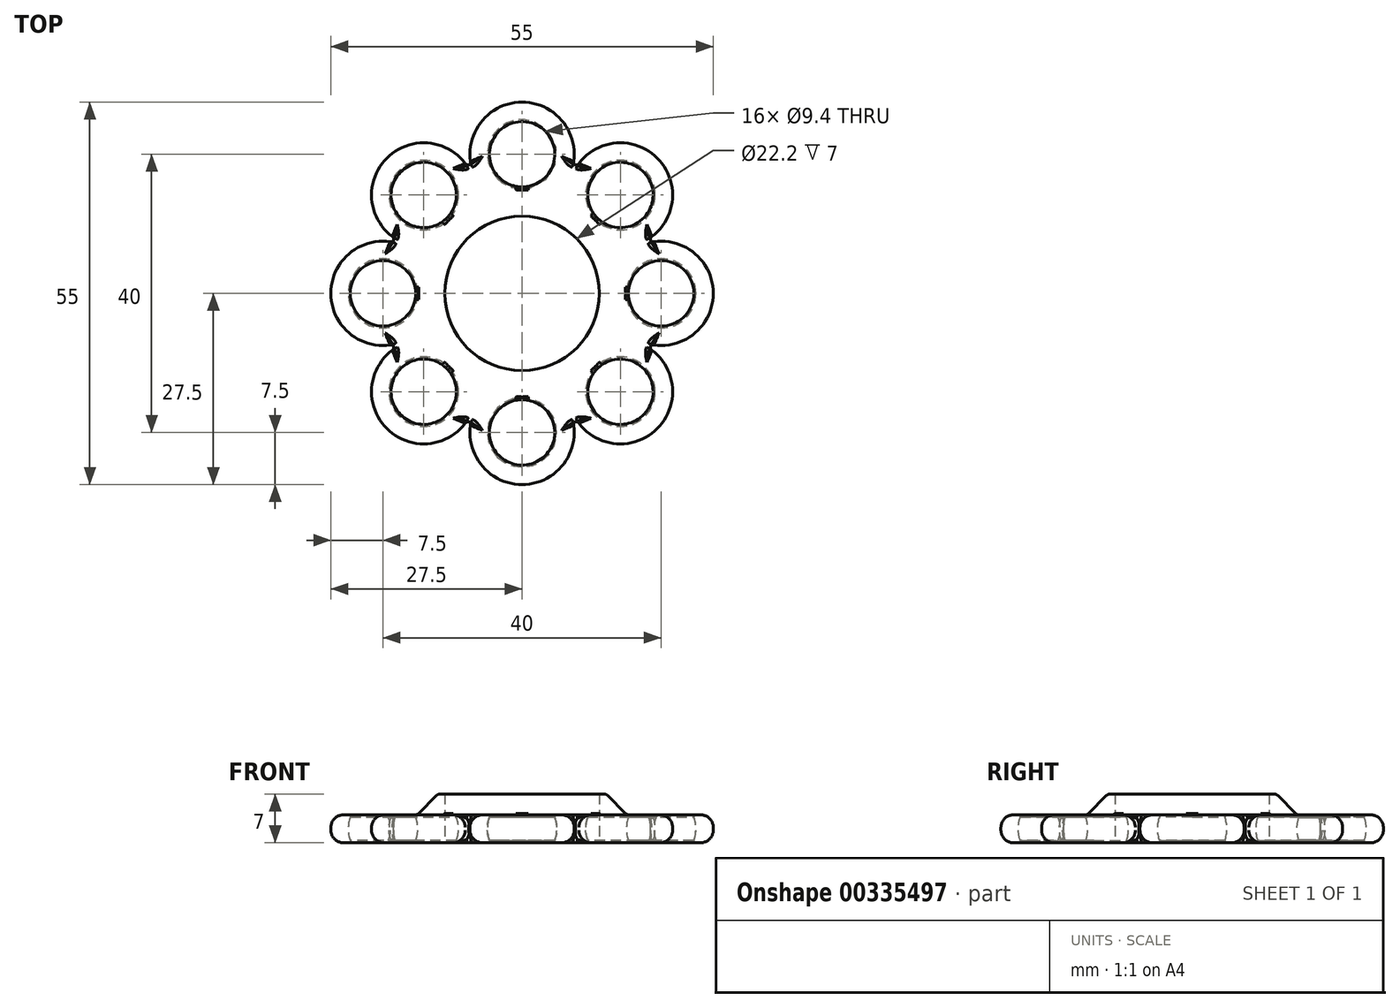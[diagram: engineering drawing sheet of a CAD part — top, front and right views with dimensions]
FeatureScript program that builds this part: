
annotation { "Feature Type Name" : "Feature", "Feature Type Description" : "" }
export const myFeature = defineFeature(function(context is Context, id is Id, definition is map)
    precondition{}
    {
        {
            var Q0;
            Q0=qCreatedBy(makeId("Top.planeOp"),FACE);
            var sketch = newSketch(context, id + "F0", { "sketchPlane" : qUnion([Q0])});
            skCircle(sketch, "E0", {"center": v(0, 0) * mm, "radius": 11.1 * mm});
            skCircle(sketch, "E1", {"center": v(0, 20) * mm, "radius": 4.7 * mm});
            skCircle(sketch, "E2.1.0", {"center": v(-14.14, 14.14) * mm, "radius": 4.7 * mm});
            skCircle(sketch, "E2.2.0", {"center": v(-20, 0) * mm, "radius": 4.7 * mm});
            skCircle(sketch, "E2.3.0", {"center": v(-14.14, -14.14) * mm, "radius": 4.7 * mm});
            skCircle(sketch, "E2.4.0", {"center": v(0, -20) * mm, "radius": 4.7 * mm});
            skCircle(sketch, "E2.5.0", {"center": v(14.14, -14.14) * mm, "radius": 4.7 * mm});
            skCircle(sketch, "E2.6.0", {"center": v(20, 0) * mm, "radius": 4.7 * mm});
            skCircle(sketch, "E2.7.0", {"center": v(14.14, 14.14) * mm, "radius": 4.7 * mm});
            skCircle(sketch, "E3", {"center": v(0, 20) * mm, "radius": 7.5 * mm});
            skCircle(sketch, "E4.1.0", {"center": v(-14.14, 14.14) * mm, "radius": 7.5 * mm});
            skCircle(sketch, "E4.2.0", {"center": v(-20, 0) * mm, "radius": 7.5 * mm});
            skCircle(sketch, "E4.3.0", {"center": v(-14.14, -14.14) * mm, "radius": 7.5 * mm});
            skCircle(sketch, "E4.4.0", {"center": v(0, -20) * mm, "radius": 7.5 * mm});
            skCircle(sketch, "E4.5.0", {"center": v(14.14, -14.14) * mm, "radius": 7.5 * mm});
            skCircle(sketch, "E4.6.0", {"center": v(20, 0) * mm, "radius": 7.5 * mm});
            skCircle(sketch, "E4.7.0", {"center": v(14.14, 14.14) * mm, "radius": 7.5 * mm});
            skCircle(sketch, "E5", {"center": v(0, 0) * mm, "radius": 20 * mm});
            skSolve(sketch);
        }
        {
            var Q0;
            Q0=makeQuery(id+"F0.imprint","IMPRINT",FACE,{"disambiguationData":[TD([[makeQuery(id+"F0.imprint","IMPRINT",EDGE,{"derivedFrom":sQuery(id+"F0.wireOp",EDGE,"E0")}),-1.0]])]});
            var Q1;
            {var subQ0=sQuery(id+"F0.wireOp",EDGE,"E5");var subQ1=sQuery(id+"F0.wireOp",EDGE,"E2.3.0");var subQ2=makeQuery(id+"F0.imprint","INTERSECT",VERTEX,{"disambiguationData":[OD(0.0)],"derivedFrom":[subQ1,subQ0]});Q1=makeQuery(id+"F0.imprint","IMPRINT",FACE,{"disambiguationData":[TD([[makeQuery(id+"F0.imprint","IMPRINT",EDGE,{"disambiguationData":[TD([[subQ2,-1.0]])],"derivedFrom":subQ1}),-1.0]])]});}
            var Q2;
            {var subQ0=sQuery(id+"F0.wireOp",EDGE,"E5");var subQ1=sQuery(id+"F0.wireOp",EDGE,"E2.3.0");var subQ2=makeQuery(id+"F0.imprint","INTERSECT",VERTEX,{"disambiguationData":[OD(0.0)],"derivedFrom":[subQ1,subQ0]});Q2=makeQuery(id+"F0.imprint","IMPRINT",FACE,{"disambiguationData":[TD([[makeQuery(id+"F0.imprint","IMPRINT",EDGE,{"disambiguationData":[TD([[subQ2,1.0]])],"derivedFrom":subQ1}),-1.0]])]});}
            var Q3;
            {var subQ0=sQuery(id+"F0.wireOp",EDGE,"E5");var subQ1=sQuery(id+"F0.wireOp",EDGE,"E2.2.0");var subQ2=makeQuery(id+"F0.imprint","INTERSECT",VERTEX,{"disambiguationData":[OD(0.0)],"derivedFrom":[subQ1,subQ0]});Q3=makeQuery(id+"F0.imprint","IMPRINT",FACE,{"disambiguationData":[TD([[makeQuery(id+"F0.imprint","IMPRINT",EDGE,{"disambiguationData":[TD([[subQ2,1.0]])],"derivedFrom":subQ1}),-1.0]])]});}
            var Q4;
            {var subQ0=sQuery(id+"F0.wireOp",EDGE,"E5");var subQ1=sQuery(id+"F0.wireOp",EDGE,"E2.2.0");var subQ2=makeQuery(id+"F0.imprint","INTERSECT",VERTEX,{"disambiguationData":[OD(0.0)],"derivedFrom":[subQ1,subQ0]});Q4=makeQuery(id+"F0.imprint","IMPRINT",FACE,{"disambiguationData":[TD([[makeQuery(id+"F0.imprint","IMPRINT",EDGE,{"disambiguationData":[TD([[subQ2,-1.0]])],"derivedFrom":subQ1}),-1.0]])]});}
            var Q5;
            {var subQ0=sQuery(id+"F0.wireOp",EDGE,"E5");var subQ1=sQuery(id+"F0.wireOp",EDGE,"E2.1.0");var subQ2=makeQuery(id+"F0.imprint","INTERSECT",VERTEX,{"disambiguationData":[OD(0.0)],"derivedFrom":[subQ1,subQ0]});Q5=makeQuery(id+"F0.imprint","IMPRINT",FACE,{"disambiguationData":[TD([[makeQuery(id+"F0.imprint","IMPRINT",EDGE,{"disambiguationData":[TD([[subQ2,-1.0]])],"derivedFrom":subQ1}),-1.0]])]});}
            var Q6;
            {var subQ0=sQuery(id+"F0.wireOp",EDGE,"E5");var subQ1=sQuery(id+"F0.wireOp",EDGE,"E2.1.0");var subQ2=makeQuery(id+"F0.imprint","INTERSECT",VERTEX,{"disambiguationData":[OD(0.0)],"derivedFrom":[subQ1,subQ0]});Q6=makeQuery(id+"F0.imprint","IMPRINT",FACE,{"disambiguationData":[TD([[makeQuery(id+"F0.imprint","IMPRINT",EDGE,{"disambiguationData":[TD([[subQ2,1.0]])],"derivedFrom":subQ1}),-1.0]])]});}
            var Q7;
            {var subQ0=sQuery(id+"F0.wireOp",EDGE,"E5");var subQ1=sQuery(id+"F0.wireOp",EDGE,"E1");var subQ2=makeQuery(id+"F0.imprint","INTERSECT",VERTEX,{"disambiguationData":[OD(0.0)],"derivedFrom":[subQ1,subQ0]});Q7=makeQuery(id+"F0.imprint","IMPRINT",FACE,{"disambiguationData":[TD([[makeQuery(id+"F0.imprint","IMPRINT",EDGE,{"disambiguationData":[TD([[subQ2,1.0]])],"derivedFrom":subQ1}),-1.0]])]});}
            var Q8;
            {var subQ0=sQuery(id+"F0.wireOp",EDGE,"E5");var subQ1=sQuery(id+"F0.wireOp",EDGE,"E1");var subQ2=makeQuery(id+"F0.imprint","INTERSECT",VERTEX,{"disambiguationData":[OD(0.0)],"derivedFrom":[subQ1,subQ0]});Q8=makeQuery(id+"F0.imprint","IMPRINT",FACE,{"disambiguationData":[TD([[makeQuery(id+"F0.imprint","IMPRINT",EDGE,{"disambiguationData":[TD([[subQ2,-1.0]])],"derivedFrom":subQ1}),-1.0]])]});}
            var Q9;
            {var subQ0=sQuery(id+"F0.wireOp",EDGE,"E5");var subQ1=sQuery(id+"F0.wireOp",EDGE,"E2.7.0");var subQ2=makeQuery(id+"F0.imprint","INTERSECT",VERTEX,{"disambiguationData":[OD(0.0)],"derivedFrom":[subQ1,subQ0]});Q9=makeQuery(id+"F0.imprint","IMPRINT",FACE,{"disambiguationData":[TD([[makeQuery(id+"F0.imprint","IMPRINT",EDGE,{"disambiguationData":[TD([[subQ2,1.0]])],"derivedFrom":subQ1}),-1.0]])]});}
            var Q10;
            {var subQ0=sQuery(id+"F0.wireOp",EDGE,"E5");var subQ1=sQuery(id+"F0.wireOp",EDGE,"E2.7.0");var subQ2=makeQuery(id+"F0.imprint","INTERSECT",VERTEX,{"disambiguationData":[OD(0.0)],"derivedFrom":[subQ1,subQ0]});Q10=makeQuery(id+"F0.imprint","IMPRINT",FACE,{"disambiguationData":[TD([[makeQuery(id+"F0.imprint","IMPRINT",EDGE,{"disambiguationData":[TD([[subQ2,-1.0]])],"derivedFrom":subQ1}),-1.0]])]});}
            var Q11;
            {var subQ0=sQuery(id+"F0.wireOp",EDGE,"E5");var subQ1=sQuery(id+"F0.wireOp",EDGE,"E2.6.0");var subQ2=makeQuery(id+"F0.imprint","INTERSECT",VERTEX,{"disambiguationData":[OD(0.0)],"derivedFrom":[subQ1,subQ0]});Q11=makeQuery(id+"F0.imprint","IMPRINT",FACE,{"disambiguationData":[TD([[makeQuery(id+"F0.imprint","IMPRINT",EDGE,{"disambiguationData":[TD([[subQ2,-1.0]])],"derivedFrom":subQ1}),-1.0]])]});}
            var Q12;
            {var subQ0=sQuery(id+"F0.wireOp",EDGE,"E5");var subQ1=sQuery(id+"F0.wireOp",EDGE,"E2.6.0");var subQ2=makeQuery(id+"F0.imprint","INTERSECT",VERTEX,{"disambiguationData":[OD(0.0)],"derivedFrom":[subQ1,subQ0]});Q12=makeQuery(id+"F0.imprint","IMPRINT",FACE,{"disambiguationData":[TD([[makeQuery(id+"F0.imprint","IMPRINT",EDGE,{"disambiguationData":[TD([[subQ2,1.0]])],"derivedFrom":subQ1}),-1.0]])]});}
            var Q13;
            {var subQ0=sQuery(id+"F0.wireOp",EDGE,"E5");var subQ1=sQuery(id+"F0.wireOp",EDGE,"E2.5.0");var subQ2=makeQuery(id+"F0.imprint","INTERSECT",VERTEX,{"disambiguationData":[OD(0.0)],"derivedFrom":[subQ1,subQ0]});Q13=makeQuery(id+"F0.imprint","IMPRINT",FACE,{"disambiguationData":[TD([[makeQuery(id+"F0.imprint","IMPRINT",EDGE,{"disambiguationData":[TD([[subQ2,1.0]])],"derivedFrom":subQ1}),-1.0]])]});}
            var Q14;
            {var subQ0=sQuery(id+"F0.wireOp",EDGE,"E5");var subQ1=sQuery(id+"F0.wireOp",EDGE,"E2.5.0");var subQ2=makeQuery(id+"F0.imprint","INTERSECT",VERTEX,{"disambiguationData":[OD(0.0)],"derivedFrom":[subQ1,subQ0]});Q14=makeQuery(id+"F0.imprint","IMPRINT",FACE,{"disambiguationData":[TD([[makeQuery(id+"F0.imprint","IMPRINT",EDGE,{"disambiguationData":[TD([[subQ2,-1.0]])],"derivedFrom":subQ1}),-1.0]])]});}
            var Q15;
            {var subQ0=sQuery(id+"F0.wireOp",EDGE,"E5");var subQ1=sQuery(id+"F0.wireOp",EDGE,"E2.4.0");var subQ2=makeQuery(id+"F0.imprint","INTERSECT",VERTEX,{"disambiguationData":[OD(0.0)],"derivedFrom":[subQ1,subQ0]});Q15=makeQuery(id+"F0.imprint","IMPRINT",FACE,{"disambiguationData":[TD([[makeQuery(id+"F0.imprint","IMPRINT",EDGE,{"disambiguationData":[TD([[subQ2,1.0]])],"derivedFrom":subQ1}),-1.0]])]});}
            var Q16;
            {var subQ0=sQuery(id+"F0.wireOp",EDGE,"E5");var subQ1=sQuery(id+"F0.wireOp",EDGE,"E2.4.0");var subQ2=makeQuery(id+"F0.imprint","INTERSECT",VERTEX,{"disambiguationData":[OD(0.0)],"derivedFrom":[subQ1,subQ0]});Q16=makeQuery(id+"F0.imprint","IMPRINT",FACE,{"disambiguationData":[TD([[makeQuery(id+"F0.imprint","IMPRINT",EDGE,{"disambiguationData":[TD([[subQ2,-1.0]])],"derivedFrom":subQ1}),-1.0]])]});}
            extrude(context, id + "F1", {"entities" : qUnion([Q0, Q1, Q2, Q3, Q4, Q5, Q6, Q7, Q8, Q9, Q10, Q11, Q12, Q13, Q14, Q15, Q16]), "depth" : 2 * mm, "hasSecondDirection" : true, "secondDirectionOppositeDirection" : true, "secondDirectionDepth" : 2 * mm});
        }
        {
            var Q0;
            Q0=makeQuery(id+"F1.opExtrude","CAP_EDGE",EDGE,{"disambiguationData":[OSD([sQuery(id+"F0.wireOp",EDGE,"E4.7.0")])],"isStart":false});
            var Q1;
            Q1=makeQuery(id+"F1.opExtrude","CAP_EDGE",EDGE,{"disambiguationData":[OSD([sQuery(id+"F0.wireOp",EDGE,"E4.7.0")])],"isStart":true});
            var Q2;
            Q2=makeQuery(id+"F1.opExtrude","CAP_EDGE",EDGE,{"disambiguationData":[OSD([sQuery(id+"F0.wireOp",EDGE,"E4.3.0")])],"isStart":true});
            var Q3;
            Q3=makeQuery(id+"F1.opExtrude","CAP_EDGE",EDGE,{"disambiguationData":[OSD([sQuery(id+"F0.wireOp",EDGE,"E4.3.0")])],"isStart":false});
            var Q4;
            Q4=makeQuery(id+"F1.opExtrude","CAP_EDGE",EDGE,{"disambiguationData":[OSD([sQuery(id+"F0.wireOp",EDGE,"E4.2.0")])],"isStart":false});
            var Q5;
            Q5=makeQuery(id+"F1.opExtrude","CAP_EDGE",EDGE,{"disambiguationData":[OSD([sQuery(id+"F0.wireOp",EDGE,"E4.2.0")])],"isStart":true});
            var Q6;
            Q6=makeQuery(id+"F1.opExtrude","CAP_EDGE",EDGE,{"disambiguationData":[OSD([sQuery(id+"F0.wireOp",EDGE,"E4.4.0")])],"isStart":false});
            var Q7;
            Q7=makeQuery(id+"F1.opExtrude","CAP_EDGE",EDGE,{"disambiguationData":[OSD([sQuery(id+"F0.wireOp",EDGE,"E4.4.0")])],"isStart":true});
            var Q8;
            Q8=makeQuery(id+"F1.opExtrude","CAP_EDGE",EDGE,{"disambiguationData":[OSD([sQuery(id+"F0.wireOp",EDGE,"E4.5.0")])],"isStart":false});
            var Q9;
            Q9=makeQuery(id+"F1.opExtrude","CAP_EDGE",EDGE,{"disambiguationData":[OSD([sQuery(id+"F0.wireOp",EDGE,"E4.5.0")])],"isStart":true});
            var Q10;
            Q10=makeQuery(id+"F1.opExtrude","CAP_EDGE",EDGE,{"disambiguationData":[OSD([sQuery(id+"F0.wireOp",EDGE,"E4.6.0")])],"isStart":false});
            var Q11;
            Q11=makeQuery(id+"F1.opExtrude","CAP_EDGE",EDGE,{"disambiguationData":[OSD([sQuery(id+"F0.wireOp",EDGE,"E4.6.0")])],"isStart":true});
            var Q12;
            Q12=makeQuery(id+"F1.opExtrude","CAP_EDGE",EDGE,{"disambiguationData":[OSD([sQuery(id+"F0.wireOp",EDGE,"E3")])],"isStart":true});
            var Q13;
            Q13=makeQuery(id+"F1.opExtrude","CAP_EDGE",EDGE,{"disambiguationData":[OSD([sQuery(id+"F0.wireOp",EDGE,"E3")])],"isStart":false});
            var Q14;
            Q14=makeQuery(id+"F1.opExtrude","CAP_EDGE",EDGE,{"disambiguationData":[OSD([sQuery(id+"F0.wireOp",EDGE,"E4.1.0")])],"isStart":true});
            var Q15;
            Q15=makeQuery(id+"F1.opExtrude","CAP_EDGE",EDGE,{"disambiguationData":[OSD([sQuery(id+"F0.wireOp",EDGE,"E4.1.0")])],"isStart":false});
            fillet(context, id + "F2", {"entities" : qUnion([Q0, Q1, Q2, Q3, Q4, Q5, Q6, Q7, Q8, Q9, Q10, Q11, Q12, Q13, Q14, Q15]), "radius" : 1.8 * mm, "tangentPropagation" : true, "allowEdgeOverflow" : false});
        }
        {
            var Q0;
            {var subQ0=sQuery(id+"F0.wireOp",EDGE,"E5");var subQ1=sQuery(id+"F0.wireOp",EDGE,"E4.4.0");Q0=makeQuery(id+"F1.opExtrude","SWEPT_EDGE",EDGE,{"disambiguationData":[OSD([subQ1,subQ0]),TDD([makeQuery(id+"F0.imprint","INTERSECT",VERTEX,{"disambiguationData":[OD(0.0)],"derivedFrom":[subQ1,subQ0]})])]});}
            var Q1;
            {var subQ0=sQuery(id+"F0.wireOp",EDGE,"E5");var subQ1=sQuery(id+"F0.wireOp",EDGE,"E4.2.0");Q1=makeQuery(id+"F1.opExtrude","SWEPT_EDGE",EDGE,{"disambiguationData":[OSD([subQ1,subQ0]),TDD([makeQuery(id+"F0.imprint","INTERSECT",VERTEX,{"disambiguationData":[OD(1.0)],"derivedFrom":[subQ1,subQ0]})])]});}
            var Q2;
            {var subQ0=sQuery(id+"F0.wireOp",EDGE,"E5");var subQ1=sQuery(id+"F0.wireOp",EDGE,"E4.2.0");Q2=makeQuery(id+"F1.opExtrude","SWEPT_EDGE",EDGE,{"disambiguationData":[OSD([subQ1,subQ0]),TDD([makeQuery(id+"F0.imprint","INTERSECT",VERTEX,{"disambiguationData":[OD(0.0)],"derivedFrom":[subQ1,subQ0]})])]});}
            var Q3;
            {var subQ0=sQuery(id+"F0.wireOp",EDGE,"E5");var subQ1=sQuery(id+"F0.wireOp",EDGE,"E3");Q3=makeQuery(id+"F1.opExtrude","SWEPT_EDGE",EDGE,{"disambiguationData":[OSD([subQ1,subQ0]),TDD([makeQuery(id+"F0.imprint","INTERSECT",VERTEX,{"disambiguationData":[OD(1.0)],"derivedFrom":[subQ1,subQ0]})])]});}
            var Q4;
            {var subQ0=sQuery(id+"F0.wireOp",EDGE,"E5");var subQ1=sQuery(id+"F0.wireOp",EDGE,"E4.7.0");Q4=makeQuery(id+"F1.opExtrude","SWEPT_EDGE",EDGE,{"disambiguationData":[OSD([subQ1,subQ0]),TDD([makeQuery(id+"F0.imprint","INTERSECT",VERTEX,{"disambiguationData":[OD(1.0)],"derivedFrom":[subQ1,subQ0]})])]});}
            var Q5;
            {var subQ0=sQuery(id+"F0.wireOp",EDGE,"E5");var subQ1=sQuery(id+"F0.wireOp",EDGE,"E4.1.0");Q5=makeQuery(id+"F1.opExtrude","SWEPT_EDGE",EDGE,{"disambiguationData":[OSD([subQ1,subQ0]),TDD([makeQuery(id+"F0.imprint","INTERSECT",VERTEX,{"disambiguationData":[OD(1.0)],"derivedFrom":[subQ1,subQ0]})])]});}
            var Q6;
            {var subQ0=sQuery(id+"F0.wireOp",EDGE,"E5");var subQ1=sQuery(id+"F0.wireOp",EDGE,"E4.3.0");Q6=makeQuery(id+"F1.opExtrude","SWEPT_EDGE",EDGE,{"disambiguationData":[OSD([subQ1,subQ0]),TDD([makeQuery(id+"F0.imprint","INTERSECT",VERTEX,{"disambiguationData":[OD(0.0)],"derivedFrom":[subQ1,subQ0]})])]});}
            var Q7;
            {var subQ0=sQuery(id+"F0.wireOp",EDGE,"E5");var subQ1=sQuery(id+"F0.wireOp",EDGE,"E4.1.0");Q7=makeQuery(id+"F1.opExtrude","SWEPT_EDGE",EDGE,{"disambiguationData":[OSD([subQ1,subQ0]),TDD([makeQuery(id+"F0.imprint","INTERSECT",VERTEX,{"disambiguationData":[OD(0.0)],"derivedFrom":[subQ1,subQ0]})])]});}
            var Q8;
            {var subQ0=sQuery(id+"F0.wireOp",EDGE,"E5");var subQ1=sQuery(id+"F0.wireOp",EDGE,"E3");Q8=makeQuery(id+"F1.opExtrude","SWEPT_EDGE",EDGE,{"disambiguationData":[OSD([subQ1,subQ0]),TDD([makeQuery(id+"F0.imprint","INTERSECT",VERTEX,{"disambiguationData":[OD(0.0)],"derivedFrom":[subQ1,subQ0]})])]});}
            var Q9;
            {var subQ0=sQuery(id+"F0.wireOp",EDGE,"E5");var subQ1=sQuery(id+"F0.wireOp",EDGE,"E4.6.0");Q9=makeQuery(id+"F1.opExtrude","SWEPT_EDGE",EDGE,{"disambiguationData":[OSD([subQ1,subQ0]),TDD([makeQuery(id+"F0.imprint","INTERSECT",VERTEX,{"disambiguationData":[OD(0.0)],"derivedFrom":[subQ1,subQ0]})])]});}
            var Q10;
            {var subQ0=sQuery(id+"F0.wireOp",EDGE,"E5");var subQ1=sQuery(id+"F0.wireOp",EDGE,"E4.7.0");Q10=makeQuery(id+"F1.opExtrude","SWEPT_EDGE",EDGE,{"disambiguationData":[OSD([subQ1,subQ0]),TDD([makeQuery(id+"F0.imprint","INTERSECT",VERTEX,{"disambiguationData":[OD(0.0)],"derivedFrom":[subQ1,subQ0]})])]});}
            var Q11;
            {var subQ0=sQuery(id+"F0.wireOp",EDGE,"E5");var subQ1=sQuery(id+"F0.wireOp",EDGE,"E4.6.0");Q11=makeQuery(id+"F1.opExtrude","SWEPT_EDGE",EDGE,{"disambiguationData":[OSD([subQ1,subQ0]),TDD([makeQuery(id+"F0.imprint","INTERSECT",VERTEX,{"disambiguationData":[OD(1.0)],"derivedFrom":[subQ1,subQ0]})])]});}
            var Q12;
            {var subQ0=sQuery(id+"F0.wireOp",EDGE,"E5");var subQ1=sQuery(id+"F0.wireOp",EDGE,"E4.5.0");Q12=makeQuery(id+"F1.opExtrude","SWEPT_EDGE",EDGE,{"disambiguationData":[OSD([subQ1,subQ0]),TDD([makeQuery(id+"F0.imprint","INTERSECT",VERTEX,{"disambiguationData":[OD(1.0)],"derivedFrom":[subQ1,subQ0]})])]});}
            var Q13;
            {var subQ0=sQuery(id+"F0.wireOp",EDGE,"E5");var subQ1=sQuery(id+"F0.wireOp",EDGE,"E4.5.0");Q13=makeQuery(id+"F1.opExtrude","SWEPT_EDGE",EDGE,{"disambiguationData":[OSD([subQ1,subQ0]),TDD([makeQuery(id+"F0.imprint","INTERSECT",VERTEX,{"disambiguationData":[OD(0.0)],"derivedFrom":[subQ1,subQ0]})])]});}
            var Q14;
            {var subQ0=sQuery(id+"F0.wireOp",EDGE,"E5");var subQ1=sQuery(id+"F0.wireOp",EDGE,"E4.4.0");Q14=makeQuery(id+"F1.opExtrude","SWEPT_EDGE",EDGE,{"disambiguationData":[OSD([subQ1,subQ0]),TDD([makeQuery(id+"F0.imprint","INTERSECT",VERTEX,{"disambiguationData":[OD(1.0)],"derivedFrom":[subQ1,subQ0]})])]});}
            var Q15;
            {var subQ0=sQuery(id+"F0.wireOp",EDGE,"E5");var subQ1=sQuery(id+"F0.wireOp",EDGE,"E4.3.0");Q15=makeQuery(id+"F1.opExtrude","SWEPT_EDGE",EDGE,{"disambiguationData":[OSD([subQ1,subQ0]),TDD([makeQuery(id+"F0.imprint","INTERSECT",VERTEX,{"disambiguationData":[OD(1.0)],"derivedFrom":[subQ1,subQ0]})])]});}
            var Q16;
            {var subQ0=sQuery(id+"F0.wireOp",EDGE,"E5");Q16=makeQuery(id+"F1.opExtrude","CAP_EDGE",EDGE,{"disambiguationData":[OSD([subQ0]),TDD([makeQuery(id+"F0.imprint","IMPRINT",EDGE,{"disambiguationData":[TD([[makeQuery(id+"F0.imprint","INTERSECT",VERTEX,{"disambiguationData":[OD(1.0)],"derivedFrom":[sQuery(id+"F0.wireOp",EDGE,"E4.4.0"),subQ0]}),-1.0]])],"derivedFrom":subQ0})])],"isStart":false});}
            var Q17;
            {var subQ0=sQuery(id+"F0.wireOp",EDGE,"E5");Q17=makeQuery(id+"F1.opExtrude","CAP_EDGE",EDGE,{"disambiguationData":[OSD([subQ0]),TDD([makeQuery(id+"F0.imprint","IMPRINT",EDGE,{"disambiguationData":[TD([[makeQuery(id+"F0.imprint","INTERSECT",VERTEX,{"disambiguationData":[OD(1.0)],"derivedFrom":[sQuery(id+"F0.wireOp",EDGE,"E4.4.0"),subQ0]}),-1.0]])],"derivedFrom":subQ0})])],"isStart":true});}
            var Q18;
            {var subQ0=sQuery(id+"F0.wireOp",EDGE,"E5");Q18=makeQuery(id+"F1.opExtrude","CAP_EDGE",EDGE,{"disambiguationData":[OSD([subQ0]),TDD([makeQuery(id+"F0.imprint","IMPRINT",EDGE,{"disambiguationData":[TD([[makeQuery(id+"F0.imprint","INTERSECT",VERTEX,{"disambiguationData":[OD(1.0)],"derivedFrom":[sQuery(id+"F0.wireOp",EDGE,"E4.5.0"),subQ0]}),-1.0]])],"derivedFrom":subQ0})])],"isStart":false});}
            var Q19;
            {var subQ0=sQuery(id+"F0.wireOp",EDGE,"E5");Q19=makeQuery(id+"F1.opExtrude","CAP_EDGE",EDGE,{"disambiguationData":[OSD([subQ0]),TDD([makeQuery(id+"F0.imprint","IMPRINT",EDGE,{"disambiguationData":[TD([[makeQuery(id+"F0.imprint","INTERSECT",VERTEX,{"disambiguationData":[OD(1.0)],"derivedFrom":[sQuery(id+"F0.wireOp",EDGE,"E4.5.0"),subQ0]}),-1.0]])],"derivedFrom":subQ0})])],"isStart":true});}
            var Q20;
            {var subQ0=sQuery(id+"F0.wireOp",EDGE,"E5");Q20=makeQuery(id+"F1.opExtrude","CAP_EDGE",EDGE,{"disambiguationData":[OSD([subQ0]),TDD([makeQuery(id+"F0.imprint","IMPRINT",EDGE,{"disambiguationData":[TD([[makeQuery(id+"F0.imprint","INTERSECT",VERTEX,{"disambiguationData":[OD(1.0)],"derivedFrom":[sQuery(id+"F0.wireOp",EDGE,"E4.3.0"),subQ0]}),-1.0]])],"derivedFrom":subQ0})])],"isStart":false});}
            var Q21;
            {var subQ0=sQuery(id+"F0.wireOp",EDGE,"E5");Q21=makeQuery(id+"F1.opExtrude","CAP_EDGE",EDGE,{"disambiguationData":[OSD([subQ0]),TDD([makeQuery(id+"F0.imprint","IMPRINT",EDGE,{"disambiguationData":[TD([[makeQuery(id+"F0.imprint","INTERSECT",VERTEX,{"disambiguationData":[OD(1.0)],"derivedFrom":[sQuery(id+"F0.wireOp",EDGE,"E4.3.0"),subQ0]}),-1.0]])],"derivedFrom":subQ0})])],"isStart":true});}
            var Q22;
            {var subQ0=sQuery(id+"F0.wireOp",EDGE,"E5");Q22=makeQuery(id+"F1.opExtrude","CAP_EDGE",EDGE,{"disambiguationData":[OSD([subQ0]),TDD([makeQuery(id+"F0.imprint","IMPRINT",EDGE,{"disambiguationData":[TD([[makeQuery(id+"F0.imprint","INTERSECT",VERTEX,{"disambiguationData":[OD(1.0)],"derivedFrom":[sQuery(id+"F0.wireOp",EDGE,"E4.2.0"),subQ0]}),-1.0]])],"derivedFrom":subQ0})])],"isStart":true});}
            var Q23;
            {var subQ0=sQuery(id+"F0.wireOp",EDGE,"E5");Q23=makeQuery(id+"F1.opExtrude","CAP_EDGE",EDGE,{"disambiguationData":[OSD([subQ0]),TDD([makeQuery(id+"F0.imprint","IMPRINT",EDGE,{"disambiguationData":[TD([[makeQuery(id+"F0.imprint","INTERSECT",VERTEX,{"disambiguationData":[OD(1.0)],"derivedFrom":[sQuery(id+"F0.wireOp",EDGE,"E4.2.0"),subQ0]}),-1.0]])],"derivedFrom":subQ0})])],"isStart":false});}
            var Q24;
            {var subQ0=sQuery(id+"F0.wireOp",EDGE,"E5");Q24=makeQuery(id+"F1.opExtrude","CAP_EDGE",EDGE,{"disambiguationData":[OSD([subQ0]),TDD([makeQuery(id+"F0.imprint","IMPRINT",EDGE,{"disambiguationData":[TD([[makeQuery(id+"F0.imprint","INTERSECT",VERTEX,{"disambiguationData":[OD(1.0)],"derivedFrom":[sQuery(id+"F0.wireOp",EDGE,"E4.1.0"),subQ0]}),-1.0]])],"derivedFrom":subQ0})])],"isStart":false});}
            var Q25;
            {var subQ0=sQuery(id+"F0.wireOp",EDGE,"E5");Q25=makeQuery(id+"F1.opExtrude","CAP_EDGE",EDGE,{"disambiguationData":[OSD([subQ0]),TDD([makeQuery(id+"F0.imprint","IMPRINT",EDGE,{"disambiguationData":[TD([[makeQuery(id+"F0.imprint","INTERSECT",VERTEX,{"disambiguationData":[OD(1.0)],"derivedFrom":[sQuery(id+"F0.wireOp",EDGE,"E4.1.0"),subQ0]}),-1.0]])],"derivedFrom":subQ0})])],"isStart":true});}
            var Q26;
            {var subQ0=sQuery(id+"F0.wireOp",EDGE,"E5");Q26=makeQuery(id+"F1.opExtrude","CAP_EDGE",EDGE,{"disambiguationData":[OSD([subQ0]),TDD([makeQuery(id+"F0.imprint","IMPRINT",EDGE,{"disambiguationData":[TD([[makeQuery(id+"F0.imprint","INTERSECT",VERTEX,{"disambiguationData":[OD(1.0)],"derivedFrom":[sQuery(id+"F0.wireOp",EDGE,"E3"),subQ0]}),-1.0]])],"derivedFrom":subQ0})])],"isStart":false});}
            var Q27;
            {var subQ0=sQuery(id+"F0.wireOp",EDGE,"E5");Q27=makeQuery(id+"F1.opExtrude","CAP_EDGE",EDGE,{"disambiguationData":[OSD([subQ0]),TDD([makeQuery(id+"F0.imprint","IMPRINT",EDGE,{"disambiguationData":[TD([[makeQuery(id+"F0.imprint","INTERSECT",VERTEX,{"disambiguationData":[OD(1.0)],"derivedFrom":[sQuery(id+"F0.wireOp",EDGE,"E3"),subQ0]}),-1.0]])],"derivedFrom":subQ0})])],"isStart":true});}
            var Q28;
            {var subQ0=sQuery(id+"F0.wireOp",EDGE,"E5");Q28=makeQuery(id+"F1.opExtrude","CAP_EDGE",EDGE,{"disambiguationData":[OSD([subQ0]),TDD([makeQuery(id+"F0.imprint","IMPRINT",EDGE,{"disambiguationData":[TD([[makeQuery(id+"F0.imprint","INTERSECT",VERTEX,{"disambiguationData":[OD(0.0)],"derivedFrom":[sQuery(id+"F0.wireOp",EDGE,"E3"),subQ0]}),1.0]])],"derivedFrom":subQ0})])],"isStart":true});}
            var Q29;
            {var subQ0=sQuery(id+"F0.wireOp",EDGE,"E5");Q29=makeQuery(id+"F1.opExtrude","CAP_EDGE",EDGE,{"disambiguationData":[OSD([subQ0]),TDD([makeQuery(id+"F0.imprint","IMPRINT",EDGE,{"disambiguationData":[TD([[makeQuery(id+"F0.imprint","INTERSECT",VERTEX,{"disambiguationData":[OD(0.0)],"derivedFrom":[sQuery(id+"F0.wireOp",EDGE,"E3"),subQ0]}),1.0]])],"derivedFrom":subQ0})])],"isStart":false});}
            var Q30;
            {var subQ0=sQuery(id+"F0.wireOp",EDGE,"E5");Q30=makeQuery(id+"F1.opExtrude","CAP_EDGE",EDGE,{"disambiguationData":[OSD([subQ0]),TDD([makeQuery(id+"F0.imprint","IMPRINT",EDGE,{"disambiguationData":[TD([[makeQuery(id+"F0.imprint","INTERSECT",VERTEX,{"disambiguationData":[OD(0.0)],"derivedFrom":[sQuery(id+"F0.wireOp",EDGE,"E4.6.0"),subQ0]}),-1.0]])],"derivedFrom":subQ0})])],"isStart":false});}
            var Q31;
            {var subQ0=sQuery(id+"F0.wireOp",EDGE,"E5");Q31=makeQuery(id+"F1.opExtrude","CAP_EDGE",EDGE,{"disambiguationData":[OSD([subQ0]),TDD([makeQuery(id+"F0.imprint","IMPRINT",EDGE,{"disambiguationData":[TD([[makeQuery(id+"F0.imprint","INTERSECT",VERTEX,{"disambiguationData":[OD(0.0)],"derivedFrom":[sQuery(id+"F0.wireOp",EDGE,"E4.6.0"),subQ0]}),-1.0]])],"derivedFrom":subQ0})])],"isStart":true});}
            fillet(context, id + "F3", {"entities" : qUnion([Q0, Q1, Q2, Q3, Q4, Q5, Q6, Q7, Q8, Q9, Q10, Q11, Q12, Q13, Q14, Q15, Q16, Q17, Q18, Q19, Q20, Q21, Q22, Q23, Q24, Q25, Q26, Q27, Q28, Q29, Q30, Q31]), "radius" : .5 * mm, "tangentPropagation" : true, "allowEdgeOverflow" : false});
        }
        {
            var Q0;
            Q0=qCreatedBy(makeId("Right.planeOp"),FACE);
            var sketch = newSketch(context, id + "F4", { "sketchPlane" : qUnion([Q0])});
            skPoint(sketch, "E6.1", {"position": v(20, 0) * mm});
            skLineSegment(sketch, "E7", {"start": v(-20, 12.7) * mm, "end": v(-20, -12.9) * mm, "construction": true});
            skLineSegment(sketch, "E8", {"start": v(20, 13.15) * mm, "end": v(20.03, -12.9) * mm, "construction": true});
            skPoint(sketch, "E9", {"position": v(-20, 5) * mm});
            skArc(sketch, "E10", {"start": v(-20, 5) * mm, "mid": v(-25, 0) * mm, "end": v(-20, -5) * mm});
            skLineSegment(sketch, "E11", {"start": v(-20, 5) * mm, "end": v(-20, -5) * mm});
            skLineSegment(sketch, "E12", {"start": v(0, 41.23) * mm, "end": v(0, -49.38) * mm, "construction": true});
            skArc(sketch, "E13", {"start": v(20.02, -5) * mm, "mid": v(25, 0) * mm, "end": v(20, 5) * mm});
            skLineSegment(sketch, "E14", {"start": v(20, 5) * mm, "end": v(20.02, -5) * mm});
            skSolve(sketch);
        }
        {
            var Q0;
            Q0=makeQuery(id+"F4.imprint","IMPRINT",FACE,{"disambiguationData":[TD([[makeQuery(id+"F4.imprint","IMPRINT",EDGE,{"derivedFrom":sQuery(id+"F4.wireOp",EDGE,"E10")}),1.0]])]});
            var Q1;
            Q1=sQuery(id+"F4.wireOp",EDGE,"E7");
            revolve(context, id + "F5", {"entities" : qUnion([Q0]), "axis" : qUnion([Q1]), "revolveType" : RevolveType.FULL});
        }
        {
            var Q0;
            Q0=makeQuery(id+"F4.imprint","IMPRINT",FACE,{"disambiguationData":[TD([[makeQuery(id+"F4.imprint","IMPRINT",EDGE,{"derivedFrom":sQuery(id+"F4.wireOp",EDGE,"E13")}),1.0]])]});
            var Q1;
            Q1=sQuery(id+"F4.wireOp",EDGE,"E8");
            revolve(context, id + "F6", {"entities" : qUnion([Q0]), "axis" : qUnion([Q1]), "revolveType" : RevolveType.FULL});
        }
        {
            var Q0;
            Q0=makeQuery(id+"F5.opRevolve","SWEPT_BODY",BODY,{"disambiguationData":[OSD([sQuery(id+"F4.wireOp",EDGE,"E10"),sQuery(id+"F4.wireOp",EDGE,"E11")])]});
            var Q1;
            Q1=makeQuery(id+"F6.opRevolve","SWEPT_BODY",BODY,{"disambiguationData":[OSD([sQuery(id+"F4.wireOp",EDGE,"E13"),sQuery(id+"F4.wireOp",EDGE,"E14")])]});
            var Q2;
            Q2=makeQuery(id+"F1.opExtrude","SWEPT_BODY",BODY,{"disambiguationData":[OSD([sQuery(id+"F0.wireOp",EDGE,"E0"),sQuery(id+"F0.wireOp",EDGE,"E1"),sQuery(id+"F0.wireOp",EDGE,"E2.1.0"),sQuery(id+"F0.wireOp",EDGE,"E2.2.0"),sQuery(id+"F0.wireOp",EDGE,"E2.3.0"),sQuery(id+"F0.wireOp",EDGE,"E2.4.0"),sQuery(id+"F0.wireOp",EDGE,"E2.5.0"),sQuery(id+"F0.wireOp",EDGE,"E2.6.0"),sQuery(id+"F0.wireOp",EDGE,"E2.7.0"),sQuery(id+"F0.wireOp",EDGE,"E3"),sQuery(id+"F0.wireOp",EDGE,"E4.1.0"),sQuery(id+"F0.wireOp",EDGE,"E4.2.0"),sQuery(id+"F0.wireOp",EDGE,"E4.3.0"),sQuery(id+"F0.wireOp",EDGE,"E4.4.0"),sQuery(id+"F0.wireOp",EDGE,"E4.5.0"),sQuery(id+"F0.wireOp",EDGE,"E4.6.0"),sQuery(id+"F0.wireOp",EDGE,"E4.7.0"),sQuery(id+"F0.wireOp",EDGE,"E5")])]});
            booleanBodies(context, id + "F7", {"operationType" : BooleanOperationType.SUBTRACTION, "tools" : qUnion([Q0, Q1]), "targets" : qUnion([Q2])});
        }
        {
            var Q0;
            Q0=qCreatedBy(makeId("Front.planeOp"),FACE);
            var sketch = newSketch(context, id + "F8", { "sketchPlane" : qUnion([Q0])});
            skPoint(sketch, "E15.0", {"position": v(-20, 0) * mm});
            skPoint(sketch, "E15.1", {"position": v(20, 0) * mm});
            skLineSegment(sketch, "E16", {"start": v(-20, 19.56) * mm, "end": v(-20, -19.6) * mm, "construction": true});
            skLineSegment(sketch, "E17", {"start": v(20, 20.64) * mm, "end": v(20, -20.78) * mm, "construction": true});
            skArc(sketch, "E18", {"start": v(-20, 5) * mm, "mid": v(-25, 0) * mm, "end": v(-20, -5) * mm});
            skLineSegment(sketch, "E19", {"start": v(-20, 5) * mm, "end": v(-20, -5) * mm});
            skArc(sketch, "E20", {"start": v(20, -5) * mm, "mid": v(25, 0) * mm, "end": v(20, 5) * mm});
            skLineSegment(sketch, "E21", {"start": v(20, 5) * mm, "end": v(20, -5) * mm});
            skSolve(sketch);
        }
        {
            var Q0;
            Q0=makeQuery(id+"F8.imprint","IMPRINT",FACE,{"disambiguationData":[TD([[makeQuery(id+"F8.imprint","IMPRINT",EDGE,{"derivedFrom":sQuery(id+"F8.wireOp",EDGE,"E18")}),1.0]])]});
            var Q1;
            Q1=sQuery(id+"F8.wireOp",EDGE,"E16");
            revolve(context, id + "F9", {"entities" : qUnion([Q0]), "axis" : qUnion([Q1]), "revolveType" : RevolveType.FULL});
        }
        {
            var Q0;
            Q0=makeQuery(id+"F8.imprint","IMPRINT",FACE,{"disambiguationData":[TD([[makeQuery(id+"F8.imprint","IMPRINT",EDGE,{"derivedFrom":sQuery(id+"F8.wireOp",EDGE,"E20")}),1.0]])]});
            var Q1;
            Q1=sQuery(id+"F8.wireOp",EDGE,"E21");
            revolve(context, id + "F10", {"entities" : qUnion([Q0]), "axis" : qUnion([Q1]), "revolveType" : RevolveType.FULL});
        }
        {
            var Q0;
            Q0=makeQuery(id+"F9.opRevolve","SWEPT_BODY",BODY,{"disambiguationData":[OSD([sQuery(id+"F8.wireOp",EDGE,"E18"),sQuery(id+"F8.wireOp",EDGE,"E19")])]});
            var Q1;
            Q1=makeQuery(id+"F10.opRevolve","SWEPT_BODY",BODY,{"disambiguationData":[OSD([sQuery(id+"F8.wireOp",EDGE,"E20"),sQuery(id+"F8.wireOp",EDGE,"E21")])]});
            var Q2;
            Q2=makeQuery(id+"F1.opExtrude","SWEPT_BODY",BODY,{"disambiguationData":[OSD([sQuery(id+"F0.wireOp",EDGE,"E0"),sQuery(id+"F0.wireOp",EDGE,"E1"),sQuery(id+"F0.wireOp",EDGE,"E2.1.0"),sQuery(id+"F0.wireOp",EDGE,"E2.2.0"),sQuery(id+"F0.wireOp",EDGE,"E2.3.0"),sQuery(id+"F0.wireOp",EDGE,"E2.4.0"),sQuery(id+"F0.wireOp",EDGE,"E2.5.0"),sQuery(id+"F0.wireOp",EDGE,"E2.6.0"),sQuery(id+"F0.wireOp",EDGE,"E2.7.0"),sQuery(id+"F0.wireOp",EDGE,"E3"),sQuery(id+"F0.wireOp",EDGE,"E4.1.0"),sQuery(id+"F0.wireOp",EDGE,"E4.2.0"),sQuery(id+"F0.wireOp",EDGE,"E4.3.0"),sQuery(id+"F0.wireOp",EDGE,"E4.4.0"),sQuery(id+"F0.wireOp",EDGE,"E4.5.0"),sQuery(id+"F0.wireOp",EDGE,"E4.6.0"),sQuery(id+"F0.wireOp",EDGE,"E4.7.0"),sQuery(id+"F0.wireOp",EDGE,"E5")])]});
            booleanBodies(context, id + "F11", {"operationType" : BooleanOperationType.SUBTRACTION, "tools" : qUnion([Q0, Q1]), "targets" : qUnion([Q2])});
        }
        {
            var Q0;
            Q0=qCreatedBy(makeId("Front.planeOp"),FACE);
            var Q1;
            Q1=sQuery(id+"F0.wireOp",VERTEX,"E2.3.0.center");
            cPlane(context, id + "F12", {"entities" : qUnion([Q0, Q1]), "cplaneType" : CPlaneType.PLANE_POINT, "offset" : 25 * mm, "width" : 150 * mm, "height" : 150 * mm});
        }
        {
            var Q0;
            Q0=qCreatedBy(id+"F12.planeOp",FACE);
            var sketch = newSketch(context, id + "F13", { "sketchPlane" : qUnion([Q0])});
            skPoint(sketch, "E22.0", {"position": v(-14.14, 0) * mm});
            skPoint(sketch, "E22.1", {"position": v(14.14, 0) * mm});
            skLineSegment(sketch, "E23", {"start": v(-14.14, 21.06) * mm, "end": v(-14.14, -25.17) * mm, "construction": true});
            skLineSegment(sketch, "E24", {"start": v(14.14, 18.25) * mm, "end": v(14.14, -22.97) * mm, "construction": true});
            skPoint(sketch, "E25", {"position": v(-14.14, 5) * mm});
            skPoint(sketch, "E26", {"position": v(-14.14, -5) * mm});
            skPoint(sketch, "E27", {"position": v(14.14, -5) * mm});
            skPoint(sketch, "E28", {"position": v(14.14, 5) * mm});
            skArc(sketch, "E29", {"start": v(-14.14, 5) * mm, "mid": v(-19.14, 0) * mm, "end": v(-14.14, -5) * mm});
            skArc(sketch, "E30", {"start": v(14.14, -5) * mm, "mid": v(19.14, 0) * mm, "end": v(14.14, 5) * mm});
            skLineSegment(sketch, "E31", {"start": v(-14.14, 5) * mm, "end": v(-14.14, -5) * mm});
            skLineSegment(sketch, "E32", {"start": v(14.14, 5) * mm, "end": v(14.14, -5) * mm});
            skSolve(sketch);
        }
        {
            var Q0;
            Q0=makeQuery(id+"F13.imprint","IMPRINT",FACE,{"disambiguationData":[TD([[makeQuery(id+"F13.imprint","IMPRINT",EDGE,{"derivedFrom":sQuery(id+"F13.wireOp",EDGE,"E29")}),1.0]])]});
            var Q1;
            Q1=sQuery(id+"F13.wireOp",EDGE,"E23");
            revolve(context, id + "F14", {"entities" : qUnion([Q0]), "axis" : qUnion([Q1]), "revolveType" : RevolveType.FULL});
        }
        {
            var Q0;
            Q0=makeQuery(id+"F13.imprint","IMPRINT",FACE,{"disambiguationData":[TD([[makeQuery(id+"F13.imprint","IMPRINT",EDGE,{"derivedFrom":sQuery(id+"F13.wireOp",EDGE,"E30")}),1.0]])]});
            var Q1;
            Q1=sQuery(id+"F13.wireOp",EDGE,"E24");
            revolve(context, id + "F15", {"entities" : qUnion([Q0]), "axis" : qUnion([Q1]), "revolveType" : RevolveType.FULL});
        }
        {
            var Q0;
            Q0=makeQuery(id+"F15.opRevolve","SWEPT_BODY",BODY,{"disambiguationData":[OSD([sQuery(id+"F13.wireOp",EDGE,"E30"),sQuery(id+"F13.wireOp",EDGE,"E32")])]});
            var Q1;
            Q1=makeQuery(id+"F14.opRevolve","SWEPT_BODY",BODY,{"disambiguationData":[OSD([sQuery(id+"F13.wireOp",EDGE,"E29"),sQuery(id+"F13.wireOp",EDGE,"E31")])]});
            var Q2;
            Q2=makeQuery(id+"F1.opExtrude","SWEPT_BODY",BODY,{"disambiguationData":[OSD([sQuery(id+"F0.wireOp",EDGE,"E0"),sQuery(id+"F0.wireOp",EDGE,"E1"),sQuery(id+"F0.wireOp",EDGE,"E2.1.0"),sQuery(id+"F0.wireOp",EDGE,"E2.2.0"),sQuery(id+"F0.wireOp",EDGE,"E2.3.0"),sQuery(id+"F0.wireOp",EDGE,"E2.4.0"),sQuery(id+"F0.wireOp",EDGE,"E2.5.0"),sQuery(id+"F0.wireOp",EDGE,"E2.6.0"),sQuery(id+"F0.wireOp",EDGE,"E2.7.0"),sQuery(id+"F0.wireOp",EDGE,"E3"),sQuery(id+"F0.wireOp",EDGE,"E4.1.0"),sQuery(id+"F0.wireOp",EDGE,"E4.2.0"),sQuery(id+"F0.wireOp",EDGE,"E4.3.0"),sQuery(id+"F0.wireOp",EDGE,"E4.4.0"),sQuery(id+"F0.wireOp",EDGE,"E4.5.0"),sQuery(id+"F0.wireOp",EDGE,"E4.6.0"),sQuery(id+"F0.wireOp",EDGE,"E4.7.0"),sQuery(id+"F0.wireOp",EDGE,"E5")])]});
            booleanBodies(context, id + "F16", {"operationType" : BooleanOperationType.SUBTRACTION, "tools" : qUnion([Q0, Q1]), "targets" : qUnion([Q2])});
        }
        {
            var Q0;
            Q0=qCreatedBy(makeId("Front.planeOp"),FACE);
            var Q1;
            Q1=sQuery(id+"F0.wireOp",VERTEX,"E4.7.0.center");
            cPlane(context, id + "F17", {"entities" : qUnion([Q0, Q1]), "cplaneType" : CPlaneType.PLANE_POINT, "offset" : 25 * mm, "width" : 150 * mm, "height" : 150 * mm});
        }
        {
            var Q0;
            Q0=qCreatedBy(id+"F17.planeOp",FACE);
            var sketch = newSketch(context, id + "F18", { "sketchPlane" : qUnion([Q0])});
            skPoint(sketch, "E33.0", {"position": v(14.14, 0) * mm});
            skPoint(sketch, "E33.1", {"position": v(-14.14, 0) * mm});
            skLineSegment(sketch, "E34", {"start": v(14.14, 20.99) * mm, "end": v(14.14, -18.6) * mm, "construction": true});
            skLineSegment(sketch, "E35", {"start": v(-14.14, 22.52) * mm, "end": v(-14.14, -18.6) * mm, "construction": true});
            skPoint(sketch, "E36", {"position": v(14.14, 5) * mm});
            skPoint(sketch, "E37", {"position": v(-14.14, 5) * mm});
            skPoint(sketch, "E38", {"position": v(14.14, -5) * mm});
            skPoint(sketch, "E39", {"position": v(-14.14, -5) * mm});
            skArc(sketch, "E40", {"start": v(14.14, -5) * mm, "mid": v(19.14, 0) * mm, "end": v(14.14, 5) * mm});
            skArc(sketch, "E41", {"start": v(-14.14, 5) * mm, "mid": v(-19.14, 0) * mm, "end": v(-14.14, -5) * mm});
            skLineSegment(sketch, "E42", {"start": v(14.14, 5) * mm, "end": v(14.14, -5) * mm});
            skLineSegment(sketch, "E43", {"start": v(-14.14, 5) * mm, "end": v(-14.14, -5) * mm});
            skSolve(sketch);
        }
        {
            var Q0;
            Q0=makeQuery(id+"F18.imprint","IMPRINT",FACE,{"disambiguationData":[TD([[makeQuery(id+"F18.imprint","IMPRINT",EDGE,{"derivedFrom":sQuery(id+"F18.wireOp",EDGE,"E40")}),1.0]])]});
            var Q1;
            Q1=sQuery(id+"F18.wireOp",EDGE,"E34");
            revolve(context, id + "F19", {"entities" : qUnion([Q0]), "axis" : qUnion([Q1]), "revolveType" : RevolveType.FULL});
        }
        {
            var Q0;
            Q0=makeQuery(id+"F18.imprint","IMPRINT",FACE,{"disambiguationData":[TD([[makeQuery(id+"F18.imprint","IMPRINT",EDGE,{"derivedFrom":sQuery(id+"F18.wireOp",EDGE,"E41")}),1.0]])]});
            var Q1;
            Q1=sQuery(id+"F18.wireOp",EDGE,"E35");
            revolve(context, id + "F20", {"entities" : qUnion([Q0]), "axis" : qUnion([Q1]), "revolveType" : RevolveType.FULL});
        }
        {
            var Q0;
            Q0=makeQuery(id+"F20.opRevolve","SWEPT_BODY",BODY,{"disambiguationData":[OSD([sQuery(id+"F18.wireOp",EDGE,"E41"),sQuery(id+"F18.wireOp",EDGE,"E43")])]});
            var Q1;
            Q1=makeQuery(id+"F19.opRevolve","SWEPT_BODY",BODY,{"disambiguationData":[OSD([sQuery(id+"F18.wireOp",EDGE,"E40"),sQuery(id+"F18.wireOp",EDGE,"E42")])]});
            var Q2;
            Q2=makeQuery(id+"F1.opExtrude","SWEPT_BODY",BODY,{"disambiguationData":[OSD([sQuery(id+"F0.wireOp",EDGE,"E0"),sQuery(id+"F0.wireOp",EDGE,"E1"),sQuery(id+"F0.wireOp",EDGE,"E2.1.0"),sQuery(id+"F0.wireOp",EDGE,"E2.2.0"),sQuery(id+"F0.wireOp",EDGE,"E2.3.0"),sQuery(id+"F0.wireOp",EDGE,"E2.4.0"),sQuery(id+"F0.wireOp",EDGE,"E2.5.0"),sQuery(id+"F0.wireOp",EDGE,"E2.6.0"),sQuery(id+"F0.wireOp",EDGE,"E2.7.0"),sQuery(id+"F0.wireOp",EDGE,"E3"),sQuery(id+"F0.wireOp",EDGE,"E4.1.0"),sQuery(id+"F0.wireOp",EDGE,"E4.2.0"),sQuery(id+"F0.wireOp",EDGE,"E4.3.0"),sQuery(id+"F0.wireOp",EDGE,"E4.4.0"),sQuery(id+"F0.wireOp",EDGE,"E4.5.0"),sQuery(id+"F0.wireOp",EDGE,"E4.6.0"),sQuery(id+"F0.wireOp",EDGE,"E4.7.0"),sQuery(id+"F0.wireOp",EDGE,"E5")])]});
            booleanBodies(context, id + "F21", {"operationType" : BooleanOperationType.SUBTRACTION, "tools" : qUnion([Q0, Q1]), "targets" : qUnion([Q2])});
        }
        {
            var Q0;
            Q0=makeQuery(id+"F1.opExtrude","CAP_FACE",FACE,{"disambiguationData":[OSD([sQuery(id+"F0.wireOp",EDGE,"E0"),sQuery(id+"F0.wireOp",EDGE,"E1"),sQuery(id+"F0.wireOp",EDGE,"E2.1.0"),sQuery(id+"F0.wireOp",EDGE,"E2.2.0"),sQuery(id+"F0.wireOp",EDGE,"E2.3.0"),sQuery(id+"F0.wireOp",EDGE,"E2.4.0"),sQuery(id+"F0.wireOp",EDGE,"E2.5.0"),sQuery(id+"F0.wireOp",EDGE,"E2.6.0"),sQuery(id+"F0.wireOp",EDGE,"E2.7.0"),sQuery(id+"F0.wireOp",EDGE,"E3"),sQuery(id+"F0.wireOp",EDGE,"E4.1.0"),sQuery(id+"F0.wireOp",EDGE,"E4.2.0"),sQuery(id+"F0.wireOp",EDGE,"E4.3.0"),sQuery(id+"F0.wireOp",EDGE,"E4.4.0"),sQuery(id+"F0.wireOp",EDGE,"E4.5.0"),sQuery(id+"F0.wireOp",EDGE,"E4.6.0"),sQuery(id+"F0.wireOp",EDGE,"E4.7.0"),sQuery(id+"F0.wireOp",EDGE,"E5")])],"isStart":false});
            var sketch = newSketch(context, id + "F22", { "sketchPlane" : qUnion([Q0])});
            skCircle(sketch, "E44.0", {"center": v(0, 0) * mm, "radius": 11.1 * mm});
            skCircle(sketch, "E45.0", {"center": v(0, 0) * mm, "radius": 15.1 * mm});
            skSolve(sketch);
        }
        {
            var Q0;
            Q0=makeQuery(id+"F22.imprint","IMPRINT",FACE,{"disambiguationData":[TD([[makeQuery(id+"F22.imprint","IMPRINT",EDGE,{"derivedFrom":sQuery(id+"F22.wireOp",EDGE,"E44.0")}),-1.0]])]});
            extrude(context, id + "F23", {"entities" : qUnion([Q0]), "operationType" : NewBodyOperationType.ADD, "depth" : 3 * mm});
        }
        {
            var Q0;
            Q0=makeQuery(id+"F23.opExtrude","CAP_EDGE",EDGE,{"disambiguationData":[OSD([sQuery(id+"F22.wireOp",EDGE,"E45.0")])],"isStart":false});
            chamfer(context, id + "F24", {"entities" : qUnion([Q0]), "width" : 3 * mm, "tangentPropagation" : true});
        }
        {
            var Q0;
            Q0=makeQuery(id+"F24.opChamfer","BLEND_EDGE",EDGE,{"blendedFrom":[makeQuery(id+"F23.opExtrude","CAP_EDGE",EDGE,{"disambiguationData":[OSD([sQuery(id+"F22.wireOp",EDGE,"E45.0")])],"isStart":false}),makeQuery(id+"F1.opExtrude","CAP_FACE",FACE,{"disambiguationData":[OSD([sQuery(id+"F0.wireOp",EDGE,"E0"),sQuery(id+"F0.wireOp",EDGE,"E1"),sQuery(id+"F0.wireOp",EDGE,"E2.1.0"),sQuery(id+"F0.wireOp",EDGE,"E2.2.0"),sQuery(id+"F0.wireOp",EDGE,"E2.3.0"),sQuery(id+"F0.wireOp",EDGE,"E2.4.0"),sQuery(id+"F0.wireOp",EDGE,"E2.5.0"),sQuery(id+"F0.wireOp",EDGE,"E2.6.0"),sQuery(id+"F0.wireOp",EDGE,"E2.7.0"),sQuery(id+"F0.wireOp",EDGE,"E3"),sQuery(id+"F0.wireOp",EDGE,"E4.1.0"),sQuery(id+"F0.wireOp",EDGE,"E4.2.0"),sQuery(id+"F0.wireOp",EDGE,"E4.3.0"),sQuery(id+"F0.wireOp",EDGE,"E4.4.0"),sQuery(id+"F0.wireOp",EDGE,"E4.5.0"),sQuery(id+"F0.wireOp",EDGE,"E4.6.0"),sQuery(id+"F0.wireOp",EDGE,"E4.7.0"),sQuery(id+"F0.wireOp",EDGE,"E5")])],"isStart":false})],"blendedInto":[makeQuery(id+"F1.opExtrude","CAP_FACE",FACE,{"disambiguationData":[OSD([sQuery(id+"F0.wireOp",EDGE,"E0"),sQuery(id+"F0.wireOp",EDGE,"E1"),sQuery(id+"F0.wireOp",EDGE,"E2.1.0"),sQuery(id+"F0.wireOp",EDGE,"E2.2.0"),sQuery(id+"F0.wireOp",EDGE,"E2.3.0"),sQuery(id+"F0.wireOp",EDGE,"E2.4.0"),sQuery(id+"F0.wireOp",EDGE,"E2.5.0"),sQuery(id+"F0.wireOp",EDGE,"E2.6.0"),sQuery(id+"F0.wireOp",EDGE,"E2.7.0"),sQuery(id+"F0.wireOp",EDGE,"E3"),sQuery(id+"F0.wireOp",EDGE,"E4.1.0"),sQuery(id+"F0.wireOp",EDGE,"E4.2.0"),sQuery(id+"F0.wireOp",EDGE,"E4.3.0"),sQuery(id+"F0.wireOp",EDGE,"E4.4.0"),sQuery(id+"F0.wireOp",EDGE,"E4.5.0"),sQuery(id+"F0.wireOp",EDGE,"E4.6.0"),sQuery(id+"F0.wireOp",EDGE,"E4.7.0"),sQuery(id+"F0.wireOp",EDGE,"E5")])],"isStart":false})]});
            var Q1;
            {var subQ0=sQuery(id+"F22.wireOp",EDGE,"E45.0");Q1=makeQuery(id+"F24.opChamfer","BLEND_EDGE",EDGE,{"blendedFrom":[makeQuery(id+"F23.opExtrude","CAP_EDGE",EDGE,{"disambiguationData":[OSD([subQ0])],"isStart":false}),makeQuery(id+"F23.opExtrude","CAP_FACE",FACE,{"disambiguationData":[OSD([sQuery(id+"F22.wireOp",EDGE,"E44.0"),subQ0])],"isStart":false})],"blendedInto":[makeQuery(id+"F23.opExtrude","CAP_FACE",FACE,{"disambiguationData":[OSD([sQuery(id+"F22.wireOp",EDGE,"E44.0"),subQ0])],"isStart":false})]});}
            fillet(context, id + "F25", {"entities" : qUnion([Q0, Q1]), "radius" : .75 * mm, "tangentPropagation" : true, "allowEdgeOverflow" : false});
        }
    });
